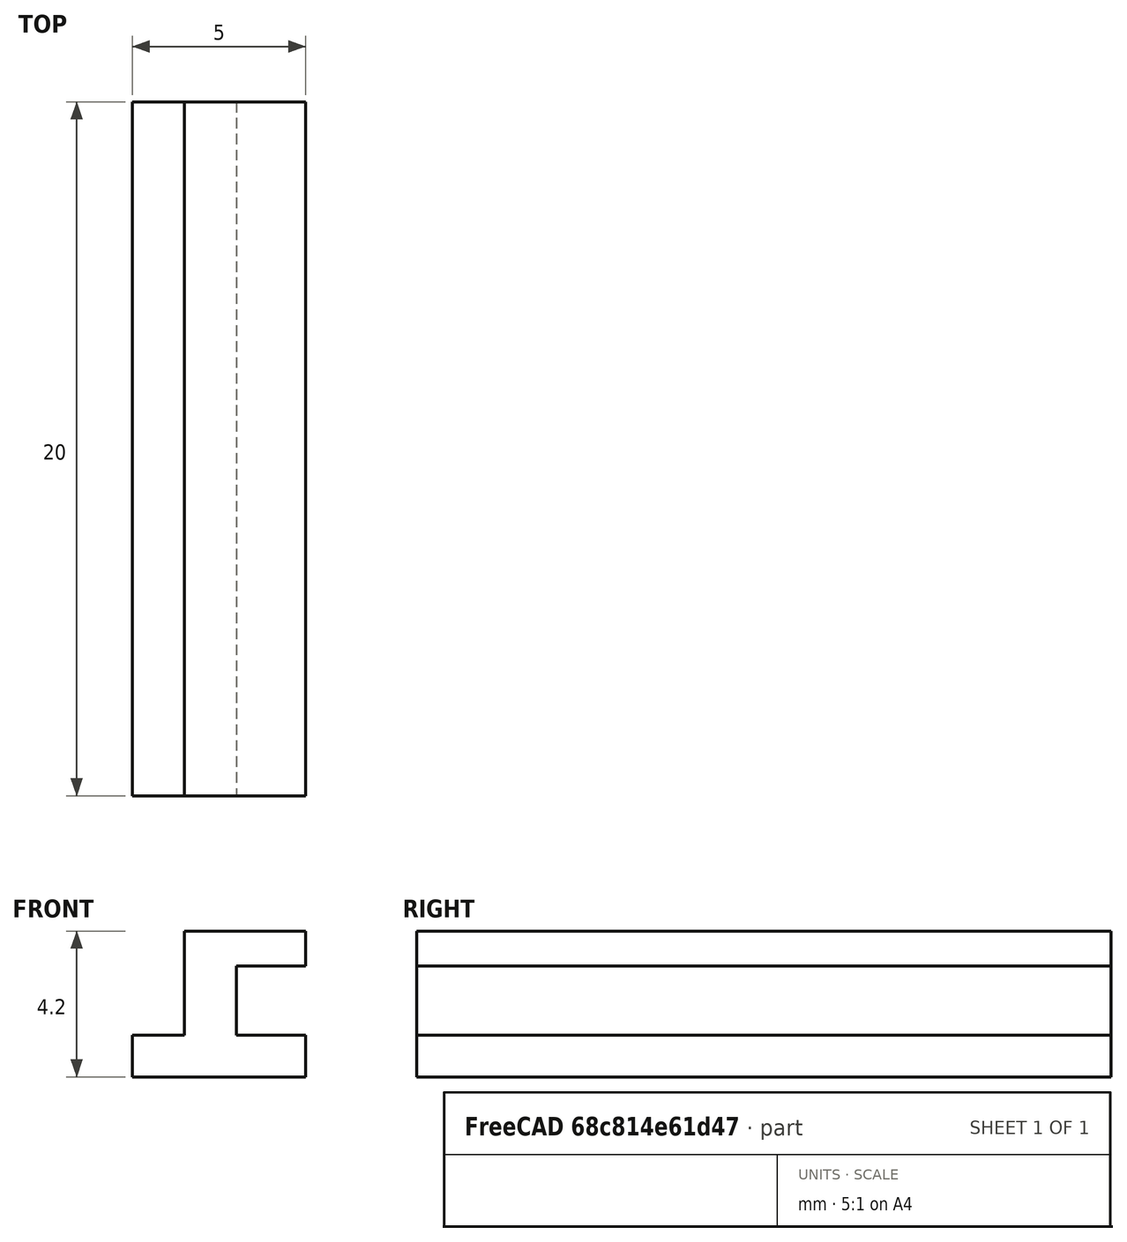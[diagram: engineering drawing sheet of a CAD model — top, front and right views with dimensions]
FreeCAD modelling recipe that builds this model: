
FCSTD DOCUMENT  (FreeCAD 0.18R16146 (Git))
Label: Al_extruded_box_PCB_clips
License: All rights reserved
LicenseURL: http://en.wikipedia.org/wiki/All_rights_reserved
objects: Sketcher::SketchObject×1, PartDesign::Pad×1, PartDesign::Body×1
note: 4 computed .brp shape members not serialized (recipe doc carries the construction recipe); baked Part::Feature solids carry a one-line shape summary decoded from their .brp

FEATURE [Sketcher::SketchObject] Sketch  label="PCB_holder_outline_sketch"
  MapMode = 5
  Placement = pos=(0,0,0) rot=(1,0,0;1.5708rad)
  Support = -> [XZ_Plane]
  sketch-geometry (10):
    g0: LineSegment StartX=0 StartY=0 StartZ=0 EndX=5 EndY=0 EndZ=0
    g1: LineSegment StartX=5 StartY=0 StartZ=0 EndX=5 EndY=1.2 EndZ=0
    g2: LineSegment StartX=5 StartY=1.2 StartZ=0 EndX=3 EndY=1.2 EndZ=0
    g3: LineSegment StartX=3 StartY=1.2 StartZ=0 EndX=3 EndY=3.2 EndZ=0
    g4: LineSegment StartX=3 StartY=3.2 StartZ=0 EndX=5 EndY=3.2 EndZ=0
    g5: LineSegment StartX=5 StartY=3.2 StartZ=0 EndX=5 EndY=4.2 EndZ=0
    g6: LineSegment StartX=5 StartY=4.2 StartZ=0 EndX=1.5 EndY=4.2 EndZ=0
    g7: LineSegment StartX=1.5 StartY=4.2 StartZ=0 EndX=1.5 EndY=1.2 EndZ=0
    g8: LineSegment StartX=1.5 StartY=1.2 StartZ=0 EndX=0 EndY=1.2 EndZ=0
    g9: LineSegment StartX=0 StartY=1.2 StartZ=0 EndX=0 EndY=0 EndZ=0
  constraints (29):
    c: Coincident(g-1,g0)
    c: Horizontal(g0)
    c: Coincident(g0,g1)
    c: Vertical(g1)
    c: Coincident(g1,g2)
    c: Horizontal(g2)
    c: Coincident(g2,g3)
    c: Vertical(g3)
    c: Coincident(g3,g4)
    c: Horizontal(g4)
    c: Coincident(g4,g5)
    c: Vertical(g5)
    c: Coincident(g5,g6)
    c: Horizontal(g6)
    c: Coincident(g6,g7)
    c: Vertical(g7)
    c: Coincident(g7,g8)
    c: Horizontal(g8)
    c: Coincident(g8,g9)
    c: Coincident(g9,g0)
    c: Vertical(g9)
    c: DistanceX(g0,g0) = 5
    c: DistanceY(g9,g9) = 1.2
    c: DistanceY(g1,g1) = 1.2
    c: DistanceY(g3,g3) = 2
    c: DistanceX(g8,g8) = 1.5
    c: DistanceY(g7,g7) = 3
    c: Vertical(g4,g0)
    c: DistanceX(g8,g2) = 3
FEATURE [PartDesign::Pad] Pad  label="PCB holder pad"
  Length = 20
  Length2 = 100
  Placement = pos=(0,0,0) rot=(1,0,0;1.5708rad)
  Profile = -> Sketch
  Type = 0
FEATURE [PartDesign::Body] Body
  Group = -> [Sketch,Pad]
  Origin = -> Origin
  Tip = -> Pad
